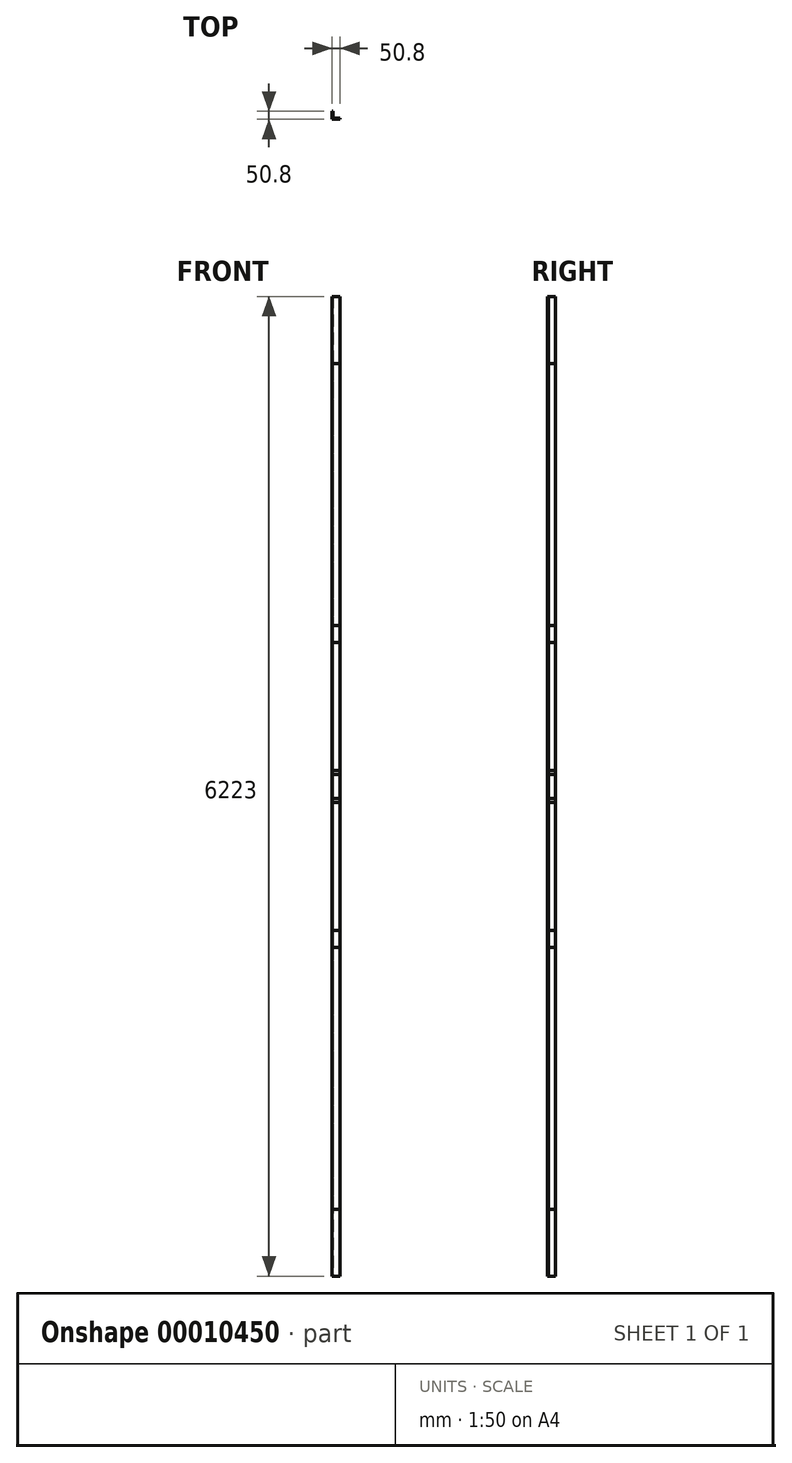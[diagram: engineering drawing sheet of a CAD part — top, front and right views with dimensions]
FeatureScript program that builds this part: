
annotation { "Feature Type Name" : "Feature", "Feature Type Description" : "" }
export const myFeature = defineFeature(function(context is Context, id is Id, definition is map)
    precondition{}
    {
        {
            var Q0;
            Q0=qCreatedBy(makeId("Top.planeOp"),FACE);
            var sketch = newSketch(context, id + "F0", { "sketchPlane" : qUnion([Q0])});
            skLineSegment(sketch, "E0", {"start": v(0, 0) * mm, "end": v(50.8, 0) * mm});
            skLineSegment(sketch, "E1", {"start": v(50.8, 0) * mm, "end": v(50.8, 6.35) * mm});
            skLineSegment(sketch, "E2", {"start": v(50.8, 6.35) * mm, "end": v(12.7, 6.35) * mm});
            skLineSegment(sketch, "E3", {"start": v(6.35, 12.7) * mm, "end": v(6.35, 50.8) * mm});
            skLineSegment(sketch, "E4", {"start": v(6.35, 50.8) * mm, "end": v(0, 50.8) * mm});
            skLineSegment(sketch, "E5", {"start": v(0, 50.8) * mm, "end": v(0, 0) * mm});
            skPoint(sketch, "E6.visualSharp", {"position": v(6.35, 6.35) * mm});
            skArc(sketch, "E6.filletArc", {"start": v(6.35, 12.7) * mm, "mid": v(8.2, 8.2) * mm, "end": v(12.7, 6.35) * mm});
            skSolve(sketch);
        }
        {
            var Q0;
            Q0=makeQuery(id+"F0.imprint","IMPRINT",FACE,{"disambiguationData":[TD([[makeQuery(id+"F0.imprint","IMPRINT",EDGE,{"derivedFrom":sQuery(id+"F0.wireOp",EDGE,"E0")}),1.0]])]});
            extrude(context, id + "F1", {"entities" : qUnion([Q0]), "endBound" : BoundingType.SYMMETRIC, "depth" : 6223 * mm});
        }
        {
            var Q0;
            Q0=makeQuery(id+"F0.imprint","IMPRINT",FACE,{"disambiguationData":[TD([[makeQuery(id+"F0.imprint","IMPRINT",EDGE,{"derivedFrom":sQuery(id+"F0.wireOp",EDGE,"E0")}),1.0]])]});
            extrude(context, id + "F2", {"entities" : qUnion([Q0]), "endBound" : BoundingType.SYMMETRIC, "depth" : 5372.1 * mm});
        }
        {
            var Q0;
            Q0 = qSketchRegion(id + "F0", true);
            var Q1;
            Q1 = qBodyType(qCreatedBy(id + "F0" ,EDGE), BodyType.WIRE);
            extrude(context, id + "F3", {"entities" : qUnion([Q0]), "surfaceEntities" : qUnion([Q1]), "endBound" : BoundingType.SYMMETRIC, "depth" : 1828.8 * mm});
        }
        {
            var Q0;
            Q0 = qSketchRegion(id + "F0", true);
            var Q1;
            Q1 = qBodyType(qCreatedBy(id + "F0" ,EDGE), BodyType.WIRE);
            extrude(context, id + "F4", {"entities" : qUnion([Q0]), "surfaceEntities" : qUnion([Q1]), "endBound" : BoundingType.SYMMETRIC, "depth" : 2044.7 * mm});
        }
        {
            var Q0;
            Q0 = qSketchRegion(id + "F0", true);
            extrude(context, id + "F5", {"entities" : qUnion([Q0]), "endBound" : BoundingType.SYMMETRIC, "depth" : 203.2 * mm});
        }
        {
            var Q0;
            Q0 = qSketchRegion(id + "F0", true);
            extrude(context, id + "F6", {"entities" : qUnion([Q0]), "endBound" : BoundingType.SYMMETRIC, "depth" : 152.4 * mm});
        }
    });
